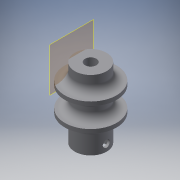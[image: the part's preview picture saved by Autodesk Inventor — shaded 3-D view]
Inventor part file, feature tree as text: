
AUTODESK INVENTOR PART (.ipt)
format: ipt  version: 2016 (Build 200138000, 138)  size: 228,864 bytes
history: native  units: mm
features: sketch x4, extrude x3, fillet x3, projected_geometry x2, revolve x1, plane x1
ambient origin geometry x8: Origin, YZ Plane, XZ Plane, XY Plane, X Axis, Y Axis, Z Axis, Center Point
bodies: Body1 (feature_tree)
feature tree (14):
  revolve  "Revolution1"  [1 undecoded]
  extrude  "Extrusion2"  Depth=5.7mm
  sketch  "Sketch3"  dims[d13=20.0mm d14=0.0mm d18=3.0mm]
  plane  "Work Plane2"
  extrude  "Extrusion6"  Depth=20.0mm
  extrude  "Extrusion7"  Depth=4.0mm
  fillet  "Fillet5"  Radius=35.0mm
  fillet  "Fillet6"  Radius=2.0mm
  fillet  "Fillet7"  Radius=2.0mm
  sketch  "Sketch1"  dims[d5=8.0mm d8=10.0mm]
  sketch  "Sketch2"  dims[d10=90.0deg d12=5.7mm]
  projected_geometry  "Projected Loop1"
  sketch  "Sketch5"  dims[d19=5.9mm d29=0.5mm d33=35.0mm d35=2.0mm d36=2.0mm d37=5.0mm d38=13.0mm d42=8.0mm d43=3.799804mm d44=7.0mm d45=0.0mm d46=3.5mm d47=2.95mm d48=3.5mm d49=7.0mm d50=0.0mm d51=4.0mm d52=4.0mm d53=4.0mm]
  projected_geometry  "Projected Loop3"
note: 1 required parameter value undecoded (feature->parameter linkage not recoverable at this tier; creation-order binding heuristic only, values carry confidence <= 0.55)
